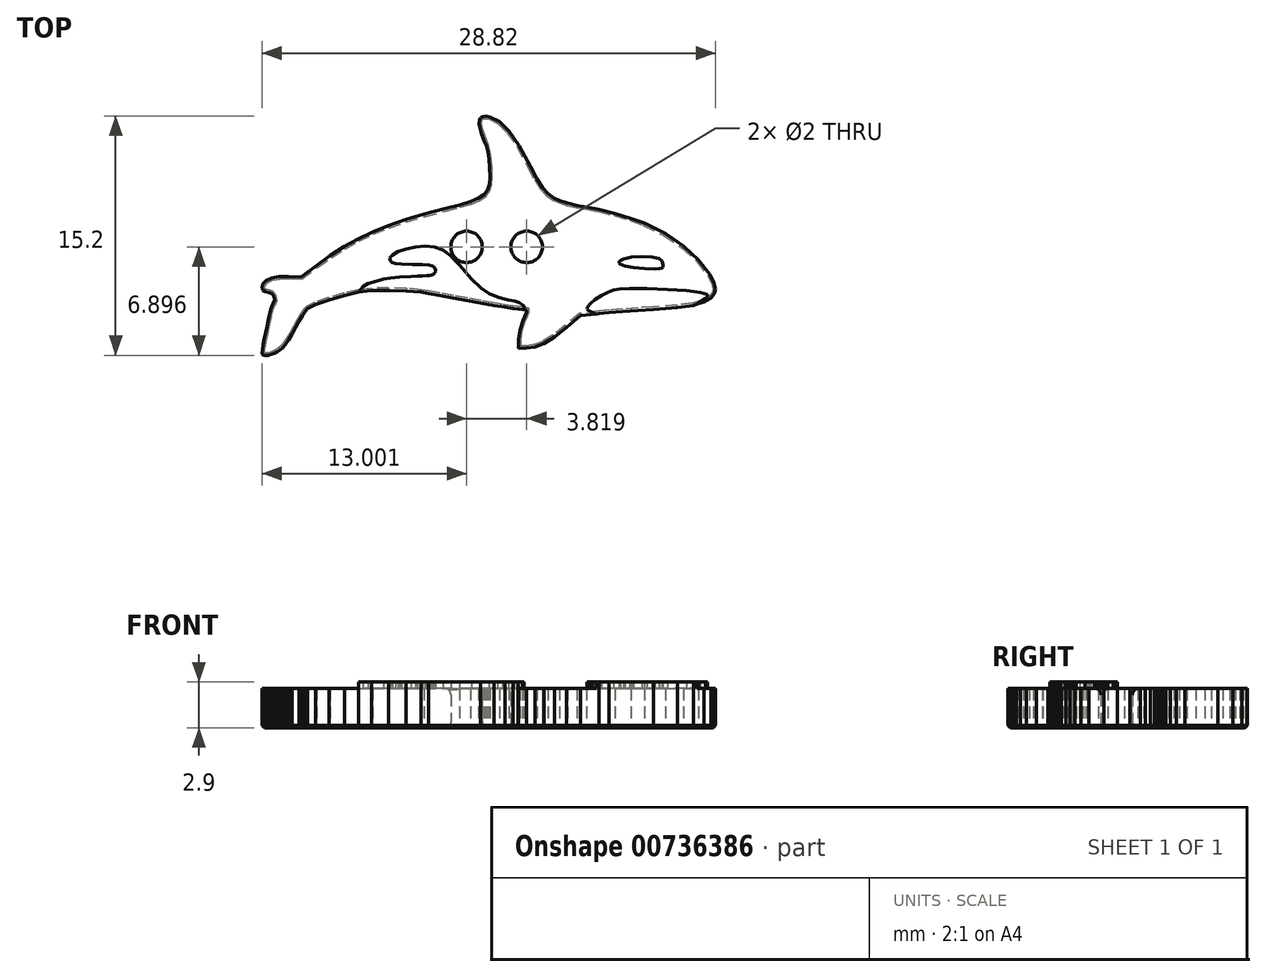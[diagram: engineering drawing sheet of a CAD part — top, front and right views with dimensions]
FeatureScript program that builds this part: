
annotation { "Feature Type Name" : "Feature", "Feature Type Description" : "" }
export const myFeature = defineFeature(function(context is Context, id is Id, definition is map)
    precondition{}
    {
        {
            var Q0;
            Q0=qCreatedBy(makeId("Top.planeOp"),FACE);
            var sketch = newSketch(context, id + "F0", { "sketchPlane" : qUnion([Q0])});
            skLineSegment(sketch, "E0", {"start": v(-14.38, -1.12) * mm, "end": v(-14.38, -1.01) * mm});
            skLineSegment(sketch, "E1", {"start": v(-14.38, -1.01) * mm, "end": v(-14.36, -0.8) * mm});
            skLineSegment(sketch, "E2", {"start": v(-14.36, -0.8) * mm, "end": v(-14.3, -0.5) * mm});
            skLineSegment(sketch, "E3", {"start": v(-14.3, -0.5) * mm, "end": v(-14.24, -0.16) * mm});
            skLineSegment(sketch, "E4", {"start": v(-14.24, -0.16) * mm, "end": v(-14.15, 0.22) * mm});
            skLineSegment(sketch, "E5", {"start": v(-14.15, 0.22) * mm, "end": v(-14.07, 0.63) * mm});
            skLineSegment(sketch, "E6", {"start": v(-14.07, 0.63) * mm, "end": v(-13.99, 1.01) * mm});
            skLineSegment(sketch, "E7", {"start": v(-13.99, 1.01) * mm, "end": v(-13.93, 1.32) * mm});
            skLineSegment(sketch, "E8", {"start": v(-13.93, 1.32) * mm, "end": v(-13.88, 1.57) * mm});
            skLineSegment(sketch, "E9", {"start": v(-13.88, 1.57) * mm, "end": v(-13.8, 1.8) * mm});
            skLineSegment(sketch, "E10", {"start": v(-13.8, 1.8) * mm, "end": v(-13.74, 1.98) * mm});
            skLineSegment(sketch, "E11", {"start": v(-13.74, 1.98) * mm, "end": v(-13.66, 2.1) * mm});
            skLineSegment(sketch, "E12", {"start": v(-13.66, 2.1) * mm, "end": v(-13.57, 2.32) * mm});
            skLineSegment(sketch, "E13", {"start": v(-13.57, 2.32) * mm, "end": v(-13.62, 2.55) * mm});
            skLineSegment(sketch, "E14", {"start": v(-13.62, 2.55) * mm, "end": v(-13.76, 2.74) * mm});
            skLineSegment(sketch, "E15", {"start": v(-13.76, 2.74) * mm, "end": v(-13.98, 2.82) * mm});
            skLineSegment(sketch, "E16", {"start": v(-13.98, 2.82) * mm, "end": v(-14.2, 2.86) * mm});
            skLineSegment(sketch, "E17", {"start": v(-14.2, 2.86) * mm, "end": v(-14.34, 2.98) * mm});
            skLineSegment(sketch, "E18", {"start": v(-14.34, 2.98) * mm, "end": v(-14.39, 3.14) * mm});
            skLineSegment(sketch, "E19", {"start": v(-14.39, 3.14) * mm, "end": v(-14.33, 3.34) * mm});
            skLineSegment(sketch, "E20", {"start": v(-14.33, 3.34) * mm, "end": v(-14.12, 3.58) * mm});
            skLineSegment(sketch, "E21", {"start": v(-14.12, 3.58) * mm, "end": v(-13.77, 3.74) * mm});
            skLineSegment(sketch, "E22", {"start": v(-13.77, 3.74) * mm, "end": v(-13.3, 3.83) * mm});
            skLineSegment(sketch, "E23", {"start": v(-13.3, 3.83) * mm, "end": v(-12.7, 3.84) * mm});
            skLineSegment(sketch, "E24", {"start": v(-12.7, 3.84) * mm, "end": v(-11.91, 3.8) * mm});
            skLineSegment(sketch, "E25", {"start": v(-11.91, 3.8) * mm, "end": v(-10.93, 4.53) * mm});
            skLineSegment(sketch, "E26", {"start": v(-10.93, 4.53) * mm, "end": v(-10.05, 5.16) * mm});
            skLineSegment(sketch, "E27", {"start": v(-10.05, 5.16) * mm, "end": v(-9.18, 5.71) * mm});
            skLineSegment(sketch, "E28", {"start": v(-9.18, 5.71) * mm, "end": v(-8.28, 6.2) * mm});
            skLineSegment(sketch, "E29", {"start": v(-8.28, 6.2) * mm, "end": v(-7.35, 6.65) * mm});
            skLineSegment(sketch, "E30", {"start": v(-7.35, 6.65) * mm, "end": v(-6.35, 7.06) * mm});
            skLineSegment(sketch, "E31", {"start": v(-6.35, 7.06) * mm, "end": v(-5.27, 7.43) * mm});
            skLineSegment(sketch, "E32", {"start": v(-5.27, 7.43) * mm, "end": v(-4.08, 7.79) * mm});
            skLineSegment(sketch, "E33", {"start": v(-4.08, 7.79) * mm, "end": v(-2.75, 8.13) * mm});
            skLineSegment(sketch, "E34", {"start": v(-2.75, 8.13) * mm, "end": v(-1.84, 8.37) * mm});
            skLineSegment(sketch, "E35", {"start": v(-1.84, 8.37) * mm, "end": v(-1.14, 8.58) * mm});
            skLineSegment(sketch, "E36", {"start": v(-1.14, 8.58) * mm, "end": v(-0.62, 8.8) * mm});
            skLineSegment(sketch, "E37", {"start": v(-0.62, 8.8) * mm, "end": v(-0.27, 9.03) * mm});
            skLineSegment(sketch, "E38", {"start": v(-0.27, 9.03) * mm, "end": v(-0.05, 9.32) * mm});
            skLineSegment(sketch, "E39", {"start": v(-0.05, 9.32) * mm, "end": v(0.06, 9.69) * mm});
            skLineSegment(sketch, "E40", {"start": v(0.06, 9.69) * mm, "end": v(0.1, 10.15) * mm});
            skLineSegment(sketch, "E41", {"start": v(0.1, 10.15) * mm, "end": v(0.07, 10.74) * mm});
            skLineSegment(sketch, "E42", {"start": v(0.07, 10.74) * mm, "end": v(0.02, 11.29) * mm});
            skLineSegment(sketch, "E43", {"start": v(0.02, 11.29) * mm, "end": v(-0.04, 11.72) * mm});
            skLineSegment(sketch, "E44", {"start": v(-0.04, 11.72) * mm, "end": v(-0.13, 12.1) * mm});
            skLineSegment(sketch, "E45", {"start": v(-0.13, 12.1) * mm, "end": v(-0.27, 12.45) * mm});
            skLineSegment(sketch, "E46", {"start": v(-0.27, 12.45) * mm, "end": v(-0.44, 12.88) * mm});
            skLineSegment(sketch, "E47", {"start": v(-0.44, 12.88) * mm, "end": v(-0.54, 13.24) * mm});
            skLineSegment(sketch, "E48", {"start": v(-0.54, 13.24) * mm, "end": v(-0.6, 13.53) * mm});
            skLineSegment(sketch, "E49", {"start": v(-0.6, 13.53) * mm, "end": v(-0.57, 13.76) * mm});
            skLineSegment(sketch, "E50", {"start": v(-0.57, 13.76) * mm, "end": v(-0.5, 13.9) * mm});
            skLineSegment(sketch, "E51", {"start": v(-0.5, 13.9) * mm, "end": v(-0.35, 14) * mm});
            skLineSegment(sketch, "E52", {"start": v(-0.35, 14) * mm, "end": v(-0.15, 14) * mm});
            skLineSegment(sketch, "E53", {"start": v(-0.15, 14) * mm, "end": v(0.12, 13.96) * mm});
            skLineSegment(sketch, "E54", {"start": v(0.12, 13.96) * mm, "end": v(0.71, 13.66) * mm});
            skLineSegment(sketch, "E55", {"start": v(0.71, 13.66) * mm, "end": v(1.3, 13.07) * mm});
            skLineSegment(sketch, "E56", {"start": v(1.3, 13.07) * mm, "end": v(1.94, 12.14) * mm});
            skLineSegment(sketch, "E57", {"start": v(1.94, 12.14) * mm, "end": v(2.66, 10.82) * mm});
            skLineSegment(sketch, "E58", {"start": v(2.66, 10.82) * mm, "end": v(3.08, 10.03) * mm});
            skLineSegment(sketch, "E59", {"start": v(3.08, 10.03) * mm, "end": v(3.43, 9.48) * mm});
            skLineSegment(sketch, "E60", {"start": v(3.43, 9.48) * mm, "end": v(3.77, 9.1) * mm});
            skLineSegment(sketch, "E61", {"start": v(3.77, 9.1) * mm, "end": v(4.17, 8.81) * mm});
            skLineSegment(sketch, "E62", {"start": v(4.17, 8.81) * mm, "end": v(4.53, 8.65) * mm});
            skLineSegment(sketch, "E63", {"start": v(4.53, 8.65) * mm, "end": v(5.03, 8.49) * mm});
            skLineSegment(sketch, "E64", {"start": v(5.03, 8.49) * mm, "end": v(5.62, 8.35) * mm});
            skLineSegment(sketch, "E65", {"start": v(5.62, 8.35) * mm, "end": v(6.24, 8.24) * mm});
            skLineSegment(sketch, "E66", {"start": v(6.24, 8.24) * mm, "end": v(7.05, 8.09) * mm});
            skLineSegment(sketch, "E67", {"start": v(7.05, 8.09) * mm, "end": v(8.05, 7.83) * mm});
            skLineSegment(sketch, "E68", {"start": v(8.05, 7.83) * mm, "end": v(9.07, 7.52) * mm});
            skLineSegment(sketch, "E69", {"start": v(9.07, 7.52) * mm, "end": v(9.9, 7.21) * mm});
            skLineSegment(sketch, "E70", {"start": v(9.9, 7.21) * mm, "end": v(11.23, 6.55) * mm});
            skLineSegment(sketch, "E71", {"start": v(11.23, 6.55) * mm, "end": v(12.4, 5.76) * mm});
            skLineSegment(sketch, "E72", {"start": v(12.4, 5.76) * mm, "end": v(13.35, 4.88) * mm});
            skLineSegment(sketch, "E73", {"start": v(13.35, 4.88) * mm, "end": v(14.06, 3.94) * mm});
            skLineSegment(sketch, "E74", {"start": v(14.06, 3.94) * mm, "end": v(14.33, 3.42) * mm});
            skLineSegment(sketch, "E75", {"start": v(14.33, 3.42) * mm, "end": v(14.43, 3.04) * mm});
            skLineSegment(sketch, "E76", {"start": v(14.43, 3.04) * mm, "end": v(14.36, 2.74) * mm});
            skLineSegment(sketch, "E77", {"start": v(14.36, 2.74) * mm, "end": v(14.13, 2.47) * mm});
            skLineSegment(sketch, "E78", {"start": v(14.13, 2.47) * mm, "end": v(13.68, 2.19) * mm});
            skLineSegment(sketch, "E79", {"start": v(13.68, 2.19) * mm, "end": v(13.01, 2) * mm});
            skLineSegment(sketch, "E80", {"start": v(13.01, 2) * mm, "end": v(12, 1.85) * mm});
            skLineSegment(sketch, "E81", {"start": v(12, 1.85) * mm, "end": v(10.47, 1.74) * mm});
            skLineSegment(sketch, "E82", {"start": v(10.47, 1.74) * mm, "end": v(9.5, 1.67) * mm});
            skLineSegment(sketch, "E83", {"start": v(9.5, 1.67) * mm, "end": v(8.52, 1.6) * mm});
            skLineSegment(sketch, "E84", {"start": v(8.52, 1.6) * mm, "end": v(7.66, 1.53) * mm});
            skLineSegment(sketch, "E85", {"start": v(7.66, 1.53) * mm, "end": v(7.03, 1.47) * mm});
            skLineSegment(sketch, "E86", {"start": v(7.03, 1.47) * mm, "end": v(5.85, 1.34) * mm});
            skLineSegment(sketch, "E87", {"start": v(5.85, 1.34) * mm, "end": v(4.96, 0.59) * mm});
            skLineSegment(sketch, "E88", {"start": v(4.96, 0.59) * mm, "end": v(4.2, -0.02) * mm});
            skLineSegment(sketch, "E89", {"start": v(4.2, -0.02) * mm, "end": v(3.54, -0.43) * mm});
            skLineSegment(sketch, "E90", {"start": v(3.54, -0.43) * mm, "end": v(2.97, -0.66) * mm});
            skLineSegment(sketch, "E91", {"start": v(2.97, -0.66) * mm, "end": v(2.43, -0.73) * mm});
            skLineSegment(sketch, "E92", {"start": v(2.43, -0.73) * mm, "end": v(1.91, -0.74) * mm});
            skLineSegment(sketch, "E93", {"start": v(1.91, -0.74) * mm, "end": v(1.92, -0.17) * mm});
            skLineSegment(sketch, "E94", {"start": v(1.92, -0.17) * mm, "end": v(2, 0.41) * mm});
            skLineSegment(sketch, "E95", {"start": v(2, 0.41) * mm, "end": v(2.2, 1.02) * mm});
            skLineSegment(sketch, "E96", {"start": v(2.2, 1.02) * mm, "end": v(2.3, 1.26) * mm});
            skLineSegment(sketch, "E97", {"start": v(2.3, 1.26) * mm, "end": v(2.37, 1.46) * mm});
            skLineSegment(sketch, "E98", {"start": v(2.37, 1.46) * mm, "end": v(2.42, 1.6) * mm});
            skLineSegment(sketch, "E99", {"start": v(2.42, 1.6) * mm, "end": v(2.42, 1.67) * mm});
            skLineSegment(sketch, "E100", {"start": v(2.42, 1.67) * mm, "end": v(2.34, 1.7) * mm});
            skLineSegment(sketch, "E101", {"start": v(2.34, 1.7) * mm, "end": v(2.15, 1.73) * mm});
            skLineSegment(sketch, "E102", {"start": v(2.15, 1.73) * mm, "end": v(1.88, 1.76) * mm});
            skLineSegment(sketch, "E103", {"start": v(1.88, 1.76) * mm, "end": v(1.55, 1.8) * mm});
            skLineSegment(sketch, "E104", {"start": v(1.55, 1.8) * mm, "end": v(1.06, 1.87) * mm});
            skLineSegment(sketch, "E105", {"start": v(1.06, 1.87) * mm, "end": v(0.35, 1.99) * mm});
            skLineSegment(sketch, "E106", {"start": v(0.35, 1.99) * mm, "end": v(-0.5, 2.13) * mm});
            skLineSegment(sketch, "E107", {"start": v(-0.5, 2.13) * mm, "end": v(-1.37, 2.3) * mm});
            skLineSegment(sketch, "E108", {"start": v(-1.37, 2.3) * mm, "end": v(-2.24, 2.46) * mm});
            skLineSegment(sketch, "E109", {"start": v(-2.24, 2.46) * mm, "end": v(-3.08, 2.62) * mm});
            skLineSegment(sketch, "E110", {"start": v(-3.08, 2.62) * mm, "end": v(-3.8, 2.75) * mm});
            skLineSegment(sketch, "E111", {"start": v(-3.8, 2.75) * mm, "end": v(-4.28, 2.83) * mm});
            skLineSegment(sketch, "E112", {"start": v(-4.28, 2.83) * mm, "end": v(-5.22, 2.92) * mm});
            skLineSegment(sketch, "E113", {"start": v(-5.22, 2.92) * mm, "end": v(-6.34, 2.95) * mm});
            skLineSegment(sketch, "E114", {"start": v(-6.34, 2.95) * mm, "end": v(-7.41, 2.92) * mm});
            skLineSegment(sketch, "E115", {"start": v(-7.41, 2.92) * mm, "end": v(-8.25, 2.83) * mm});
            skLineSegment(sketch, "E116", {"start": v(-8.25, 2.83) * mm, "end": v(-9.13, 2.63) * mm});
            skLineSegment(sketch, "E117", {"start": v(-9.13, 2.63) * mm, "end": v(-10.12, 2.33) * mm});
            skLineSegment(sketch, "E118", {"start": v(-10.12, 2.33) * mm, "end": v(-10.98, 2.03) * mm});
            skLineSegment(sketch, "E119", {"start": v(-10.98, 2.03) * mm, "end": v(-11.47, 1.8) * mm});
            skLineSegment(sketch, "E120", {"start": v(-11.47, 1.8) * mm, "end": v(-11.62, 1.63) * mm});
            skLineSegment(sketch, "E121", {"start": v(-11.62, 1.63) * mm, "end": v(-11.81, 1.35) * mm});
            skLineSegment(sketch, "E122", {"start": v(-11.81, 1.35) * mm, "end": v(-12.03, 0.98) * mm});
            skLineSegment(sketch, "E123", {"start": v(-12.03, 0.98) * mm, "end": v(-12.26, 0.58) * mm});
            skLineSegment(sketch, "E124", {"start": v(-12.26, 0.58) * mm, "end": v(-12.48, 0.16) * mm});
            skLineSegment(sketch, "E125", {"start": v(-12.48, 0.16) * mm, "end": v(-12.7, -0.22) * mm});
            skLineSegment(sketch, "E126", {"start": v(-12.7, -0.22) * mm, "end": v(-12.92, -0.52) * mm});
            skLineSegment(sketch, "E127", {"start": v(-12.92, -0.52) * mm, "end": v(-13.07, -0.71) * mm});
            skLineSegment(sketch, "E128", {"start": v(-13.07, -0.71) * mm, "end": v(-13.23, -0.85) * mm});
            skLineSegment(sketch, "E129", {"start": v(-13.23, -0.85) * mm, "end": v(-13.42, -0.96) * mm});
            skLineSegment(sketch, "E130", {"start": v(-13.42, -0.96) * mm, "end": v(-13.62, -1.06) * mm});
            skLineSegment(sketch, "E131", {"start": v(-13.62, -1.06) * mm, "end": v(-13.82, -1.13) * mm});
            skLineSegment(sketch, "E132", {"start": v(-13.82, -1.13) * mm, "end": v(-14, -1.18) * mm});
            skLineSegment(sketch, "E133", {"start": v(-14, -1.18) * mm, "end": v(-14.17, -1.2) * mm});
            skLineSegment(sketch, "E134", {"start": v(-14.17, -1.2) * mm, "end": v(-14.3, -1.17) * mm});
            skLineSegment(sketch, "E135", {"start": v(-14.3, -1.17) * mm, "end": v(-14.38, -1.12) * mm});
            skLineSegment(sketch, "E136", {"start": v(13.57, 2.29) * mm, "end": v(13.78, 2.44) * mm});
            skLineSegment(sketch, "E137", {"start": v(13.78, 2.44) * mm, "end": v(13.91, 2.57) * mm});
            skLineSegment(sketch, "E138", {"start": v(13.91, 2.57) * mm, "end": v(13.9, 2.67) * mm});
            skLineSegment(sketch, "E139", {"start": v(13.9, 2.67) * mm, "end": v(13.47, 2.8) * mm});
            skLineSegment(sketch, "E140", {"start": v(13.47, 2.8) * mm, "end": v(12.57, 2.92) * mm});
            skLineSegment(sketch, "E141", {"start": v(12.57, 2.92) * mm, "end": v(11.37, 3.01) * mm});
            skLineSegment(sketch, "E142", {"start": v(11.37, 3.01) * mm, "end": v(10.06, 3.05) * mm});
            skLineSegment(sketch, "E143", {"start": v(10.06, 3.05) * mm, "end": v(8.97, 3.06) * mm});
            skLineSegment(sketch, "E144", {"start": v(8.97, 3.06) * mm, "end": v(8.32, 3.04) * mm});
            skLineSegment(sketch, "E145", {"start": v(8.32, 3.04) * mm, "end": v(7.93, 2.98) * mm});
            skLineSegment(sketch, "E146", {"start": v(7.93, 2.98) * mm, "end": v(7.61, 2.85) * mm});
            skLineSegment(sketch, "E147", {"start": v(7.61, 2.85) * mm, "end": v(7.18, 2.62) * mm});
            skLineSegment(sketch, "E148", {"start": v(7.18, 2.62) * mm, "end": v(6.78, 2.36) * mm});
            skLineSegment(sketch, "E149", {"start": v(6.78, 2.36) * mm, "end": v(6.47, 2.1) * mm});
            skLineSegment(sketch, "E150", {"start": v(6.47, 2.1) * mm, "end": v(6.29, 1.88) * mm});
            skLineSegment(sketch, "E151", {"start": v(6.29, 1.88) * mm, "end": v(6.25, 1.77) * mm});
            skLineSegment(sketch, "E152", {"start": v(6.25, 1.77) * mm, "end": v(6.3, 1.72) * mm});
            skLineSegment(sketch, "E153", {"start": v(1.93, 2.16) * mm, "end": v(1.67, 2.26) * mm});
            skLineSegment(sketch, "E154", {"start": v(1.67, 2.26) * mm, "end": v(1.29, 2.34) * mm});
            skLineSegment(sketch, "E155", {"start": v(1.29, 2.34) * mm, "end": v(0.9, 2.44) * mm});
            skLineSegment(sketch, "E156", {"start": v(0.9, 2.44) * mm, "end": v(0.57, 2.53) * mm});
            skLineSegment(sketch, "E157", {"start": v(0.57, 2.53) * mm, "end": v(0.04, 2.75) * mm});
            skLineSegment(sketch, "E158", {"start": v(0.04, 2.75) * mm, "end": v(-0.47, 3.1) * mm});
            skLineSegment(sketch, "E159", {"start": v(-0.47, 3.1) * mm, "end": v(-1.06, 3.67) * mm});
            skLineSegment(sketch, "E160", {"start": v(-1.06, 3.67) * mm, "end": v(-1.83, 4.55) * mm});
            skLineSegment(sketch, "E161", {"start": v(-1.83, 4.55) * mm, "end": v(-2.38, 5.12) * mm});
            skLineSegment(sketch, "E162", {"start": v(-2.38, 5.12) * mm, "end": v(-2.89, 5.49) * mm});
            skLineSegment(sketch, "E163", {"start": v(-2.89, 5.49) * mm, "end": v(-3.42, 5.69) * mm});
            skLineSegment(sketch, "E164", {"start": v(-3.42, 5.69) * mm, "end": v(-4.01, 5.75) * mm});
            skLineSegment(sketch, "E165", {"start": v(-4.01, 5.75) * mm, "end": v(-4.62, 5.7) * mm});
            skLineSegment(sketch, "E166", {"start": v(-4.62, 5.7) * mm, "end": v(-5.22, 5.58) * mm});
            skLineSegment(sketch, "E167", {"start": v(-5.22, 5.58) * mm, "end": v(-5.73, 5.4) * mm});
            skLineSegment(sketch, "E168", {"start": v(-5.73, 5.4) * mm, "end": v(-6.1, 5.2) * mm});
            skLineSegment(sketch, "E169", {"start": v(-6.1, 5.2) * mm, "end": v(-6.27, 5) * mm});
            skLineSegment(sketch, "E170", {"start": v(-6.27, 5) * mm, "end": v(-6.23, 4.81) * mm});
            skLineSegment(sketch, "E171", {"start": v(-6.23, 4.81) * mm, "end": v(-6.12, 4.72) * mm});
            skLineSegment(sketch, "E172", {"start": v(-6.12, 4.72) * mm, "end": v(-5.9, 4.65) * mm});
            skLineSegment(sketch, "E173", {"start": v(-5.9, 4.65) * mm, "end": v(-5.5, 4.62) * mm});
            skLineSegment(sketch, "E174", {"start": v(-5.5, 4.62) * mm, "end": v(-4.84, 4.6) * mm});
            skLineSegment(sketch, "E175", {"start": v(-4.84, 4.6) * mm, "end": v(-4.2, 4.58) * mm});
            skLineSegment(sketch, "E176", {"start": v(-4.2, 4.58) * mm, "end": v(-3.78, 4.54) * mm});
            skLineSegment(sketch, "E177", {"start": v(-3.78, 4.54) * mm, "end": v(-3.55, 4.49) * mm});
            skLineSegment(sketch, "E178", {"start": v(-3.55, 4.49) * mm, "end": v(-3.43, 4.4) * mm});
            skLineSegment(sketch, "E179", {"start": v(-3.43, 4.4) * mm, "end": v(-3.36, 4.23) * mm});
            skLineSegment(sketch, "E180", {"start": v(-3.36, 4.23) * mm, "end": v(-3.4, 4.06) * mm});
            skLineSegment(sketch, "E181", {"start": v(-3.4, 4.06) * mm, "end": v(-3.44, 4) * mm});
            skLineSegment(sketch, "E182", {"start": v(-3.44, 4) * mm, "end": v(-3.5, 3.96) * mm});
            skLineSegment(sketch, "E183", {"start": v(-3.5, 3.96) * mm, "end": v(-3.6, 3.93) * mm});
            skLineSegment(sketch, "E184", {"start": v(-3.6, 3.93) * mm, "end": v(-3.74, 3.9) * mm});
            skLineSegment(sketch, "E185", {"start": v(-3.74, 3.9) * mm, "end": v(-3.93, 3.88) * mm});
            skLineSegment(sketch, "E186", {"start": v(-3.93, 3.88) * mm, "end": v(-4.18, 3.86) * mm});
            skLineSegment(sketch, "E187", {"start": v(-4.18, 3.86) * mm, "end": v(-4.5, 3.84) * mm});
            skLineSegment(sketch, "E188", {"start": v(-4.5, 3.84) * mm, "end": v(-4.92, 3.83) * mm});
            skLineSegment(sketch, "E189", {"start": v(-4.92, 3.83) * mm, "end": v(-5.65, 3.8) * mm});
            skLineSegment(sketch, "E190", {"start": v(-5.65, 3.8) * mm, "end": v(-6.2, 3.74) * mm});
            skLineSegment(sketch, "E191", {"start": v(-6.2, 3.74) * mm, "end": v(-6.65, 3.66) * mm});
            skLineSegment(sketch, "E192", {"start": v(-6.65, 3.66) * mm, "end": v(-7.06, 3.53) * mm});
            skLineSegment(sketch, "E193", {"start": v(-7.06, 3.53) * mm, "end": v(-7.65, 3.36) * mm});
            skLineSegment(sketch, "E194", {"start": v(11.1, 4.57) * mm, "end": v(11.03, 4.8) * mm});
            skLineSegment(sketch, "E195", {"start": v(11.03, 4.8) * mm, "end": v(10.83, 4.96) * mm});
            skLineSegment(sketch, "E196", {"start": v(10.83, 4.96) * mm, "end": v(10.4, 5.06) * mm});
            skLineSegment(sketch, "E197", {"start": v(10.4, 5.06) * mm, "end": v(9.75, 5.09) * mm});
            skLineSegment(sketch, "E198", {"start": v(9.75, 5.09) * mm, "end": v(9.09, 5.04) * mm});
            skLineSegment(sketch, "E199", {"start": v(9.09, 5.04) * mm, "end": v(8.6, 4.93) * mm});
            skLineSegment(sketch, "E200", {"start": v(8.6, 4.93) * mm, "end": v(8.4, 4.85) * mm});
            skLineSegment(sketch, "E201", {"start": v(8.4, 4.85) * mm, "end": v(8.3, 4.78) * mm});
            skLineSegment(sketch, "E202", {"start": v(8.3, 4.78) * mm, "end": v(8.3, 4.7) * mm});
            skLineSegment(sketch, "E203", {"start": v(8.3, 4.7) * mm, "end": v(8.37, 4.62) * mm});
            skLineSegment(sketch, "E204", {"start": v(8.37, 4.62) * mm, "end": v(8.67, 4.5) * mm});
            skLineSegment(sketch, "E205", {"start": v(8.67, 4.5) * mm, "end": v(9.23, 4.4) * mm});
            skLineSegment(sketch, "E206", {"start": v(9.23, 4.4) * mm, "end": v(9.9, 4.32) * mm});
            skLineSegment(sketch, "E207", {"start": v(9.9, 4.32) * mm, "end": v(10.58, 4.3) * mm});
            skLineSegment(sketch, "E208", {"start": v(10.58, 4.3) * mm, "end": v(10.86, 4.32) * mm});
            skLineSegment(sketch, "E209", {"start": v(10.86, 4.32) * mm, "end": v(11.01, 4.35) * mm});
            skLineSegment(sketch, "E210", {"start": v(11.01, 4.35) * mm, "end": v(11.08, 4.43) * mm});
            skLineSegment(sketch, "E211", {"start": v(11.08, 4.43) * mm, "end": v(11.1, 4.57) * mm});
            skLineSegment(sketch, "E212", {"start": v(-7.65, 3.36) * mm, "end": v(-7.96, 3.19) * mm});
            skLineSegment(sketch, "E213", {"start": v(-8.25, 2.83) * mm, "end": v(-7.96, 3.19) * mm});
            skLineSegment(sketch, "E214", {"start": v(1.93, 2.16) * mm, "end": v(2.15, 2.06) * mm});
            skLineSegment(sketch, "E215", {"start": v(2.15, 2.06) * mm, "end": v(2.26, 1.94) * mm});
            skLineSegment(sketch, "E216", {"start": v(2.26, 1.94) * mm, "end": v(2.27, 1.82) * mm});
            skLineSegment(sketch, "E217", {"start": v(2.27, 1.82) * mm, "end": v(2.15, 1.73) * mm});
            skLineSegment(sketch, "E218", {"start": v(6.3, 1.72) * mm, "end": v(6.43, 1.62) * mm});
            skLineSegment(sketch, "E219", {"start": v(6.43, 1.62) * mm, "end": v(6.61, 1.54) * mm});
            skLineSegment(sketch, "E220", {"start": v(6.61, 1.54) * mm, "end": v(6.87, 1.45) * mm});
            skLineSegment(sketch, "E221", {"start": v(13.57, 2.29) * mm, "end": v(13.34, 2.13) * mm});
            skPoint(sketch, "E221.endSnap0", {"position": v(13.34, 2.1) * mm});
            skLineSegment(sketch, "E222", {"start": v(13.34, 2.13) * mm, "end": v(13.26, 2.06) * mm});
            skCircle(sketch, "E223", {"center": v(0, -1) * mm, "radius": 15 * mm, "construction": true});
            skPoint(sketch, "E223.third.point", {"position": v(-14.33, 3.42) * mm});
            skLineSegment(sketch, "E224", {"start": v(-16.63, -2.36) * mm, "end": v(17.74, -2.36) * mm, "construction": true});
            skLineSegment(sketch, "E225", {"start": v(14.43, 7.5) * mm, "end": v(14.43, -2.36) * mm, "construction": true});
            skLineSegment(sketch, "E226", {"start": v(-14.39, -2.52) * mm, "end": v(-14.39, 4.2) * mm, "construction": true});
            skCircle(sketch, "E227", {"center": v(1.8, 5.7) * mm, "radius": 3.91 * mm});
            skLineSegment(sketch, "E228", {"start": v(-17.57, 5.7) * mm, "end": v(16.86, 5.7) * mm, "construction": true});
            skCircle(sketch, "E229", {"center": v(2.43, 5.7) * mm, "radius": 1 * mm});
            skCircle(sketch, "E230", {"center": v(-1.39, 5.7) * mm, "radius": 1 * mm});
            skSolve(sketch);
        }
        {
            var Q0;
            {var subQ1=sQuery(id+"F0.wireOp",EDGE,"E80");Q0=makeQuery(id+"F0.imprint","IMPRINT",FACE,{"disambiguationData":[TD([[makeQuery(id+"F0.imprint","IMPRINT",EDGE,{"derivedFrom":subQ1}),-1.0]])]});}
            var Q1;
            Q1=makeQuery(id+"F0.imprint","IMPRINT",FACE,{"disambiguationData":[TD([[makeQuery(id+"F0.imprint","IMPRINT",EDGE,{"derivedFrom":sQuery(id+"F0.wireOp",EDGE,"E102")}),-1.0]])]});
            var Q2;
            Q2=makeQuery(id+"F0.imprint","IMPRINT",FACE,{"disambiguationData":[TD([[makeQuery(id+"F0.imprint","IMPRINT",EDGE,{"derivedFrom":sQuery(id+"F0.wireOp",EDGE,"E0")}),-1.0]])]});
            var Q3;
            Q3=makeQuery(id+"F0.imprint","IMPRINT",FACE,{"disambiguationData":[TD([[makeQuery(id+"F0.imprint","IMPRINT",EDGE,{"derivedFrom":sQuery(id+"F0.wireOp",EDGE,"E194")}),1.0]])]});
            var Q4;
            Q4=makeQuery(id+"F0.imprint","IMPRINT",FACE,{"disambiguationData":[TD([[makeQuery(id+"F0.imprint","IMPRINT",EDGE,{"derivedFrom":sQuery(id+"F0.wireOp",EDGE,"E153")}),-1.0]])]});
            var Q5;
            {var subQ0=sQuery(id+"F0.wireOp",EDGE,"E106");Q5=makeQuery(id+"F0.imprint","IMPRINT",FACE,{"disambiguationData":[TD([[makeQuery(id+"F0.imprint","IMPRINT",EDGE,{"derivedFrom":subQ0}),-1.0]])]});}
            var Q6;
            {var subQ1=sQuery(id+"F0.wireOp",EDGE,"E62");Q6=makeQuery(id+"F0.imprint","IMPRINT",FACE,{"disambiguationData":[TD([[makeQuery(id+"F0.imprint","IMPRINT",EDGE,{"derivedFrom":subQ1}),-1.0]])]});}
            var Q7;
            {var subQ1=sQuery(id+"F0.wireOp",EDGE,"E104");Q7=makeQuery(id+"F0.imprint","IMPRINT",FACE,{"disambiguationData":[TD([[makeQuery(id+"F0.imprint","IMPRINT",EDGE,{"derivedFrom":subQ1}),-1.0]])]});}
            var Q8;
            {var subQ0=sQuery(id+"F0.wireOp",EDGE,"E38");Q8=makeQuery(id+"F0.imprint","IMPRINT",FACE,{"disambiguationData":[TD([[makeQuery(id+"F0.imprint","IMPRINT",EDGE,{"derivedFrom":subQ0}),-1.0]])]});}
            extrude(context, id + "F1", {"entities" : qUnion([Q0, Q1, Q2, Q3, Q4, Q5, Q6, Q7, Q8]), "depth" : 2.5 * mm, "offsetDistance" : 25 * mm});
        }
        {
            var Q0;
            Q0=makeQuery(id+"F1.opExtrude","CAP_FACE",FACE,{"disambiguationData":[OSD([sQuery(id+"F0.wireOp",EDGE,"E0"),sQuery(id+"F0.wireOp",EDGE,"E1"),sQuery(id+"F0.wireOp",EDGE,"E2"),sQuery(id+"F0.wireOp",EDGE,"E3"),sQuery(id+"F0.wireOp",EDGE,"E4"),sQuery(id+"F0.wireOp",EDGE,"E5"),sQuery(id+"F0.wireOp",EDGE,"E6"),sQuery(id+"F0.wireOp",EDGE,"E7"),sQuery(id+"F0.wireOp",EDGE,"E8"),sQuery(id+"F0.wireOp",EDGE,"E9"),sQuery(id+"F0.wireOp",EDGE,"E10"),sQuery(id+"F0.wireOp",EDGE,"E11"),sQuery(id+"F0.wireOp",EDGE,"E12"),sQuery(id+"F0.wireOp",EDGE,"E13"),sQuery(id+"F0.wireOp",EDGE,"E14"),sQuery(id+"F0.wireOp",EDGE,"E15"),sQuery(id+"F0.wireOp",EDGE,"E16"),sQuery(id+"F0.wireOp",EDGE,"E17"),sQuery(id+"F0.wireOp",EDGE,"E18"),sQuery(id+"F0.wireOp",EDGE,"E19"),sQuery(id+"F0.wireOp",EDGE,"E20"),sQuery(id+"F0.wireOp",EDGE,"E21"),sQuery(id+"F0.wireOp",EDGE,"E22"),sQuery(id+"F0.wireOp",EDGE,"E23"),sQuery(id+"F0.wireOp",EDGE,"E24"),sQuery(id+"F0.wireOp",EDGE,"E25"),sQuery(id+"F0.wireOp",EDGE,"E26"),sQuery(id+"F0.wireOp",EDGE,"E27"),sQuery(id+"F0.wireOp",EDGE,"E28"),sQuery(id+"F0.wireOp",EDGE,"E29"),sQuery(id+"F0.wireOp",EDGE,"E30"),sQuery(id+"F0.wireOp",EDGE,"E31"),sQuery(id+"F0.wireOp",EDGE,"E32"),sQuery(id+"F0.wireOp",EDGE,"E33"),sQuery(id+"F0.wireOp",EDGE,"E34"),sQuery(id+"F0.wireOp",EDGE,"E35"),sQuery(id+"F0.wireOp",EDGE,"E36"),sQuery(id+"F0.wireOp",EDGE,"E37"),sQuery(id+"F0.wireOp",EDGE,"E38"),sQuery(id+"F0.wireOp",EDGE,"E39"),sQuery(id+"F0.wireOp",EDGE,"E40"),sQuery(id+"F0.wireOp",EDGE,"E41"),sQuery(id+"F0.wireOp",EDGE,"E42"),sQuery(id+"F0.wireOp",EDGE,"E43"),sQuery(id+"F0.wireOp",EDGE,"E44"),sQuery(id+"F0.wireOp",EDGE,"E45"),sQuery(id+"F0.wireOp",EDGE,"E46"),sQuery(id+"F0.wireOp",EDGE,"E47"),sQuery(id+"F0.wireOp",EDGE,"E48"),sQuery(id+"F0.wireOp",EDGE,"E49"),sQuery(id+"F0.wireOp",EDGE,"E50"),sQuery(id+"F0.wireOp",EDGE,"E51"),sQuery(id+"F0.wireOp",EDGE,"E52"),sQuery(id+"F0.wireOp",EDGE,"E53"),sQuery(id+"F0.wireOp",EDGE,"E54"),sQuery(id+"F0.wireOp",EDGE,"E55"),sQuery(id+"F0.wireOp",EDGE,"E56"),sQuery(id+"F0.wireOp",EDGE,"E57"),sQuery(id+"F0.wireOp",EDGE,"E58"),sQuery(id+"F0.wireOp",EDGE,"E59"),sQuery(id+"F0.wireOp",EDGE,"E60"),sQuery(id+"F0.wireOp",EDGE,"E61"),sQuery(id+"F0.wireOp",EDGE,"E62"),sQuery(id+"F0.wireOp",EDGE,"E63"),sQuery(id+"F0.wireOp",EDGE,"E64"),sQuery(id+"F0.wireOp",EDGE,"E65"),sQuery(id+"F0.wireOp",EDGE,"E66"),sQuery(id+"F0.wireOp",EDGE,"E67"),sQuery(id+"F0.wireOp",EDGE,"E68"),sQuery(id+"F0.wireOp",EDGE,"E69"),sQuery(id+"F0.wireOp",EDGE,"E70"),sQuery(id+"F0.wireOp",EDGE,"E71"),sQuery(id+"F0.wireOp",EDGE,"E72"),sQuery(id+"F0.wireOp",EDGE,"E73"),sQuery(id+"F0.wireOp",EDGE,"E74"),sQuery(id+"F0.wireOp",EDGE,"E75"),sQuery(id+"F0.wireOp",EDGE,"E76"),sQuery(id+"F0.wireOp",EDGE,"E77"),sQuery(id+"F0.wireOp",EDGE,"E78"),sQuery(id+"F0.wireOp",EDGE,"E79"),sQuery(id+"F0.wireOp",EDGE,"E80"),sQuery(id+"F0.wireOp",EDGE,"E81"),sQuery(id+"F0.wireOp",EDGE,"E82"),sQuery(id+"F0.wireOp",EDGE,"E83"),sQuery(id+"F0.wireOp",EDGE,"E84"),sQuery(id+"F0.wireOp",EDGE,"E85"),sQuery(id+"F0.wireOp",EDGE,"E86"),sQuery(id+"F0.wireOp",EDGE,"E87"),sQuery(id+"F0.wireOp",EDGE,"E88"),sQuery(id+"F0.wireOp",EDGE,"E89"),sQuery(id+"F0.wireOp",EDGE,"E90"),sQuery(id+"F0.wireOp",EDGE,"E91"),sQuery(id+"F0.wireOp",EDGE,"E92"),sQuery(id+"F0.wireOp",EDGE,"E93"),sQuery(id+"F0.wireOp",EDGE,"E94"),sQuery(id+"F0.wireOp",EDGE,"E95"),sQuery(id+"F0.wireOp",EDGE,"E96"),sQuery(id+"F0.wireOp",EDGE,"E97"),sQuery(id+"F0.wireOp",EDGE,"E98"),sQuery(id+"F0.wireOp",EDGE,"E99"),sQuery(id+"F0.wireOp",EDGE,"E100"),sQuery(id+"F0.wireOp",EDGE,"E101"),sQuery(id+"F0.wireOp",EDGE,"E102"),sQuery(id+"F0.wireOp",EDGE,"E103"),sQuery(id+"F0.wireOp",EDGE,"E104"),sQuery(id+"F0.wireOp",EDGE,"E105"),sQuery(id+"F0.wireOp",EDGE,"E106"),sQuery(id+"F0.wireOp",EDGE,"E107"),sQuery(id+"F0.wireOp",EDGE,"E108"),sQuery(id+"F0.wireOp",EDGE,"E109"),sQuery(id+"F0.wireOp",EDGE,"E110"),sQuery(id+"F0.wireOp",EDGE,"E111"),sQuery(id+"F0.wireOp",EDGE,"E112"),sQuery(id+"F0.wireOp",EDGE,"E113"),sQuery(id+"F0.wireOp",EDGE,"E114"),sQuery(id+"F0.wireOp",EDGE,"E115"),sQuery(id+"F0.wireOp",EDGE,"E116"),sQuery(id+"F0.wireOp",EDGE,"E117"),sQuery(id+"F0.wireOp",EDGE,"E118"),sQuery(id+"F0.wireOp",EDGE,"E119"),sQuery(id+"F0.wireOp",EDGE,"E120"),sQuery(id+"F0.wireOp",EDGE,"E121"),sQuery(id+"F0.wireOp",EDGE,"E122"),sQuery(id+"F0.wireOp",EDGE,"E123"),sQuery(id+"F0.wireOp",EDGE,"E124"),sQuery(id+"F0.wireOp",EDGE,"E125"),sQuery(id+"F0.wireOp",EDGE,"E126"),sQuery(id+"F0.wireOp",EDGE,"E127"),sQuery(id+"F0.wireOp",EDGE,"E128"),sQuery(id+"F0.wireOp",EDGE,"E129"),sQuery(id+"F0.wireOp",EDGE,"E130"),sQuery(id+"F0.wireOp",EDGE,"E131"),sQuery(id+"F0.wireOp",EDGE,"E132"),sQuery(id+"F0.wireOp",EDGE,"E133"),sQuery(id+"F0.wireOp",EDGE,"E134"),sQuery(id+"F0.wireOp",EDGE,"E135")])],"isStart":false});
            var sketch = newSketch(context, id + "F2", { "sketchPlane" : qUnion([Q0])});
            skLineSegment(sketch, "E231.0", {"start": v(2.27, 1.82) * mm, "end": v(2.15, 1.73) * mm});
            skLineSegment(sketch, "E232.0", {"start": v(2.26, 1.94) * mm, "end": v(2.27, 1.82) * mm});
            skLineSegment(sketch, "E233.0", {"start": v(2.15, 2.06) * mm, "end": v(2.26, 1.94) * mm});
            skLineSegment(sketch, "E234.0", {"start": v(1.93, 2.16) * mm, "end": v(2.15, 2.06) * mm});
            skLineSegment(sketch, "E234.3", {"start": v(1.93, 2.16) * mm, "end": v(1.67, 2.26) * mm});
            skLineSegment(sketch, "E234.4", {"start": v(1.67, 2.26) * mm, "end": v(1.29, 2.34) * mm});
            skPoint(sketch, "E234.5", {"position": v(0.9, 2.44) * mm});
            skPoint(sketch, "E234.6", {"position": v(1.48, 2.3) * mm});
            skPoint(sketch, "E234.7", {"position": v(1.1, 2.39) * mm});
            skLineSegment(sketch, "E235.1", {"start": v(1.29, 2.34) * mm, "end": v(0.9, 2.44) * mm});
            skLineSegment(sketch, "E235.2", {"start": v(0.9, 2.44) * mm, "end": v(0.57, 2.53) * mm});
            skLineSegment(sketch, "E235.3", {"start": v(0.57, 2.53) * mm, "end": v(0.04, 2.75) * mm});
            skLineSegment(sketch, "E235.4", {"start": v(0.04, 2.75) * mm, "end": v(-0.47, 3.1) * mm});
            skLineSegment(sketch, "E235.5", {"start": v(-0.47, 3.1) * mm, "end": v(-1.06, 3.67) * mm});
            skLineSegment(sketch, "E235.6", {"start": v(-1.06, 3.67) * mm, "end": v(-1.83, 4.55) * mm});
            skLineSegment(sketch, "E235.7", {"start": v(-1.83, 4.55) * mm, "end": v(-2.38, 5.12) * mm});
            skLineSegment(sketch, "E235.8", {"start": v(-2.38, 5.12) * mm, "end": v(-2.89, 5.49) * mm});
            skLineSegment(sketch, "E235.9", {"start": v(-2.89, 5.49) * mm, "end": v(-3.42, 5.69) * mm});
            skLineSegment(sketch, "E235.10", {"start": v(-3.42, 5.69) * mm, "end": v(-4.01, 5.75) * mm});
            skLineSegment(sketch, "E235.11", {"start": v(-4.01, 5.75) * mm, "end": v(-4.62, 5.7) * mm});
            skLineSegment(sketch, "E235.12", {"start": v(-4.62, 5.7) * mm, "end": v(-5.22, 5.58) * mm});
            skLineSegment(sketch, "E235.13", {"start": v(-5.22, 5.58) * mm, "end": v(-5.73, 5.4) * mm});
            skLineSegment(sketch, "E235.14", {"start": v(-5.73, 5.4) * mm, "end": v(-6.1, 5.2) * mm});
            skLineSegment(sketch, "E235.15", {"start": v(-6.1, 5.2) * mm, "end": v(-6.27, 5) * mm});
            skLineSegment(sketch, "E235.16", {"start": v(-6.27, 5) * mm, "end": v(-6.23, 4.81) * mm});
            skLineSegment(sketch, "E235.17", {"start": v(-6.12, 4.72) * mm, "end": v(-5.9, 4.65) * mm});
            skLineSegment(sketch, "E235.18", {"start": v(-6.23, 4.81) * mm, "end": v(-6.12, 4.72) * mm});
            skLineSegment(sketch, "E235.19", {"start": v(-5.9, 4.65) * mm, "end": v(-5.5, 4.62) * mm});
            skLineSegment(sketch, "E235.20", {"start": v(-5.5, 4.62) * mm, "end": v(-4.84, 4.6) * mm});
            skLineSegment(sketch, "E235.21", {"start": v(-4.84, 4.6) * mm, "end": v(-4.2, 4.58) * mm});
            skLineSegment(sketch, "E235.22", {"start": v(-4.2, 4.58) * mm, "end": v(-3.78, 4.54) * mm});
            skLineSegment(sketch, "E235.23", {"start": v(-3.78, 4.54) * mm, "end": v(-3.55, 4.49) * mm});
            skLineSegment(sketch, "E235.24", {"start": v(-3.55, 4.49) * mm, "end": v(-3.43, 4.4) * mm});
            skLineSegment(sketch, "E235.25", {"start": v(-3.43, 4.4) * mm, "end": v(-3.36, 4.23) * mm});
            skLineSegment(sketch, "E235.26", {"start": v(-3.36, 4.23) * mm, "end": v(-3.4, 4.06) * mm});
            skLineSegment(sketch, "E235.27", {"start": v(-3.4, 4.06) * mm, "end": v(-3.44, 4) * mm});
            skLineSegment(sketch, "E235.28", {"start": v(-3.44, 4) * mm, "end": v(-3.5, 3.96) * mm});
            skLineSegment(sketch, "E235.29", {"start": v(-3.5, 3.96) * mm, "end": v(-3.6, 3.93) * mm});
            skLineSegment(sketch, "E235.30", {"start": v(-3.6, 3.93) * mm, "end": v(-3.74, 3.9) * mm});
            skLineSegment(sketch, "E235.31", {"start": v(-3.74, 3.9) * mm, "end": v(-3.93, 3.88) * mm});
            skLineSegment(sketch, "E235.32", {"start": v(-3.93, 3.88) * mm, "end": v(-4.18, 3.86) * mm});
            skLineSegment(sketch, "E235.33", {"start": v(-4.18, 3.86) * mm, "end": v(-4.5, 3.84) * mm});
            skLineSegment(sketch, "E235.34", {"start": v(-4.5, 3.84) * mm, "end": v(-4.92, 3.83) * mm});
            skLineSegment(sketch, "E235.35", {"start": v(-4.92, 3.83) * mm, "end": v(-5.65, 3.8) * mm});
            skLineSegment(sketch, "E235.36", {"start": v(-5.65, 3.8) * mm, "end": v(-6.2, 3.74) * mm});
            skLineSegment(sketch, "E235.37", {"start": v(-6.2, 3.74) * mm, "end": v(-6.65, 3.66) * mm});
            skLineSegment(sketch, "E235.38", {"start": v(-6.65, 3.66) * mm, "end": v(-7.06, 3.53) * mm});
            skLineSegment(sketch, "E235.39", {"start": v(-7.06, 3.53) * mm, "end": v(-7.65, 3.36) * mm});
            skLineSegment(sketch, "E235.40", {"start": v(-7.65, 3.36) * mm, "end": v(-7.96, 3.19) * mm});
            skLineSegment(sketch, "E235.41", {"start": v(-8.25, 2.83) * mm, "end": v(-7.96, 3.19) * mm});
            skLineSegment(sketch, "E235.42", {"start": v(-7.41, 2.92) * mm, "end": v(-8.25, 2.83) * mm});
            skLineSegment(sketch, "E235.43", {"start": v(-6.34, 2.95) * mm, "end": v(-7.41, 2.92) * mm});
            skLineSegment(sketch, "E235.44", {"start": v(-5.22, 2.92) * mm, "end": v(-6.34, 2.95) * mm});
            skLineSegment(sketch, "E235.45", {"start": v(-4.28, 2.83) * mm, "end": v(-5.22, 2.92) * mm});
            skLineSegment(sketch, "E235.46", {"start": v(-3.8, 2.75) * mm, "end": v(-4.28, 2.83) * mm});
            skLineSegment(sketch, "E235.47", {"start": v(-3.08, 2.62) * mm, "end": v(-3.8, 2.75) * mm});
            skLineSegment(sketch, "E235.48", {"start": v(-2.24, 2.46) * mm, "end": v(-3.08, 2.62) * mm});
            skLineSegment(sketch, "E235.49", {"start": v(-1.37, 2.3) * mm, "end": v(-2.24, 2.46) * mm});
            skLineSegment(sketch, "E235.50", {"start": v(-0.5, 2.13) * mm, "end": v(-1.37, 2.3) * mm});
            skLineSegment(sketch, "E235.51", {"start": v(0.35, 1.99) * mm, "end": v(-0.5, 2.13) * mm});
            skLineSegment(sketch, "E235.52", {"start": v(1.06, 1.87) * mm, "end": v(0.35, 1.99) * mm});
            skLineSegment(sketch, "E235.53", {"start": v(1.55, 1.8) * mm, "end": v(1.06, 1.87) * mm});
            skLineSegment(sketch, "E235.54", {"start": v(1.88, 1.76) * mm, "end": v(1.55, 1.8) * mm});
            skLineSegment(sketch, "E235.55", {"start": v(2.15, 1.73) * mm, "end": v(1.88, 1.76) * mm});
            skPoint(sketch, "E235.61", {"position": v(-3.15, 5.59) * mm});
            skPoint(sketch, "E235.62", {"position": v(-3.72, 5.72) * mm});
            skPoint(sketch, "E235.63", {"position": v(-4.04, 2.79) * mm});
            skPoint(sketch, "E235.64", {"position": v(2.27, 1.88) * mm});
            skLineSegment(sketch, "E236.0", {"start": v(9.23, 4.4) * mm, "end": v(9.9, 4.32) * mm});
            skLineSegment(sketch, "E236.1", {"start": v(11.37, 3.01) * mm, "end": v(10.06, 3.05) * mm});
            skLineSegment(sketch, "E236.2", {"start": v(9.9, 4.32) * mm, "end": v(10.58, 4.3) * mm});
            skLineSegment(sketch, "E236.3", {"start": v(8.67, 4.5) * mm, "end": v(9.23, 4.4) * mm});
            skLineSegment(sketch, "E236.4", {"start": v(8.37, 4.62) * mm, "end": v(8.67, 4.5) * mm});
            skLineSegment(sketch, "E236.5", {"start": v(9.75, 5.09) * mm, "end": v(9.09, 5.04) * mm});
            skLineSegment(sketch, "E236.6", {"start": v(9.09, 5.04) * mm, "end": v(8.6, 4.93) * mm});
            skLineSegment(sketch, "E237.2", {"start": v(12.57, 2.92) * mm, "end": v(11.37, 3.01) * mm});
            skLineSegment(sketch, "E237.3", {"start": v(10.83, 4.96) * mm, "end": v(10.4, 5.06) * mm});
            skLineSegment(sketch, "E237.4", {"start": v(10.4, 5.06) * mm, "end": v(9.75, 5.09) * mm});
            skLineSegment(sketch, "E237.5", {"start": v(11.03, 4.8) * mm, "end": v(10.83, 4.96) * mm});
            skLineSegment(sketch, "E237.6", {"start": v(10.58, 4.3) * mm, "end": v(10.86, 4.32) * mm});
            skLineSegment(sketch, "E238.0", {"start": v(10.86, 4.32) * mm, "end": v(11.01, 4.35) * mm});
            skLineSegment(sketch, "E238.2", {"start": v(11.1, 4.57) * mm, "end": v(11.03, 4.8) * mm});
            skLineSegment(sketch, "E238.3", {"start": v(11.01, 4.35) * mm, "end": v(11.08, 4.43) * mm});
            skLineSegment(sketch, "E238.5", {"start": v(11.08, 4.43) * mm, "end": v(11.1, 4.57) * mm});
            skLineSegment(sketch, "E239.0", {"start": v(8.6, 4.93) * mm, "end": v(8.4, 4.85) * mm});
            skLineSegment(sketch, "E240.0", {"start": v(8.3, 4.7) * mm, "end": v(8.37, 4.62) * mm});
            skLineSegment(sketch, "E240.1", {"start": v(8.3, 4.78) * mm, "end": v(8.3, 4.7) * mm});
            skLineSegment(sketch, "E240.3", {"start": v(8.4, 4.85) * mm, "end": v(8.3, 4.78) * mm});
            skLineSegment(sketch, "E241.0", {"start": v(7.93, 2.98) * mm, "end": v(7.61, 2.85) * mm});
            skLineSegment(sketch, "E241.1", {"start": v(13.57, 2.29) * mm, "end": v(13.34, 2.13) * mm});
            skLineSegment(sketch, "E241.2", {"start": v(14.13, 2.47) * mm, "end": v(13.68, 2.19) * mm});
            skLineSegment(sketch, "E241.3", {"start": v(9.5, 1.67) * mm, "end": v(8.52, 1.6) * mm});
            skLineSegment(sketch, "E241.4", {"start": v(13.47, 2.8) * mm, "end": v(12.57, 2.92) * mm});
            skLineSegment(sketch, "E241.5", {"start": v(10.47, 1.74) * mm, "end": v(9.5, 1.67) * mm});
            skLineSegment(sketch, "E241.6", {"start": v(13.68, 2.19) * mm, "end": v(13.01, 2) * mm});
            skLineSegment(sketch, "E241.7", {"start": v(7.61, 2.85) * mm, "end": v(7.18, 2.62) * mm});
            skLineSegment(sketch, "E241.8", {"start": v(12, 1.85) * mm, "end": v(10.47, 1.74) * mm});
            skLineSegment(sketch, "E241.9", {"start": v(8.32, 3.04) * mm, "end": v(7.93, 2.98) * mm});
            skLineSegment(sketch, "E241.10", {"start": v(13.57, 2.29) * mm, "end": v(13.78, 2.44) * mm});
            skLineSegment(sketch, "E241.11", {"start": v(6.43, 1.62) * mm, "end": v(6.61, 1.54) * mm});
            skLineSegment(sketch, "E241.12", {"start": v(13.9, 2.67) * mm, "end": v(13.47, 2.8) * mm});
            skLineSegment(sketch, "E241.13", {"start": v(6.61, 1.54) * mm, "end": v(6.87, 1.45) * mm});
            skLineSegment(sketch, "E241.14", {"start": v(8.52, 1.6) * mm, "end": v(7.66, 1.53) * mm});
            skLineSegment(sketch, "E241.15", {"start": v(7.66, 1.53) * mm, "end": v(7.03, 1.47) * mm});
            skLineSegment(sketch, "E241.16", {"start": v(8.97, 3.06) * mm, "end": v(8.32, 3.04) * mm});
            skLineSegment(sketch, "E241.17", {"start": v(10.06, 3.05) * mm, "end": v(8.97, 3.06) * mm});
            skLineSegment(sketch, "E241.18", {"start": v(6.47, 2.1) * mm, "end": v(6.29, 1.88) * mm});
            skLineSegment(sketch, "E241.19", {"start": v(7.18, 2.62) * mm, "end": v(6.78, 2.36) * mm});
            skLineSegment(sketch, "E241.20", {"start": v(13.01, 2) * mm, "end": v(12, 1.85) * mm});
            skLineSegment(sketch, "E241.23", {"start": v(6.78, 2.36) * mm, "end": v(6.47, 2.1) * mm});
            skLineSegment(sketch, "E242.0", {"start": v(13.78, 2.44) * mm, "end": v(13.91, 2.57) * mm});
            skLineSegment(sketch, "E243.0", {"start": v(13.91, 2.57) * mm, "end": v(13.9, 2.67) * mm});
            skLineSegment(sketch, "E244.0", {"start": v(13.34, 2.13) * mm, "end": v(13.26, 2.06) * mm});
            skLineSegment(sketch, "E245.0", {"start": v(6.29, 1.88) * mm, "end": v(6.25, 1.77) * mm});
            skLineSegment(sketch, "E245.1", {"start": v(6.25, 1.77) * mm, "end": v(6.3, 1.72) * mm});
            skLineSegment(sketch, "E245.2", {"start": v(6.3, 1.72) * mm, "end": v(6.43, 1.62) * mm});
            skSolve(sketch);
        }
        {
            var Q0;
            Q0=makeQuery(id+"F2.imprint","IMPRINT",FACE,{"disambiguationData":[TD([[makeQuery(id+"F2.imprint","IMPRINT",EDGE,{"derivedFrom":sQuery(id+"F2.wireOp",EDGE,"E234.4")}),1.0]])]});
            var Q1;
            Q1=makeQuery(id+"F2.imprint","IMPRINT",FACE,{"disambiguationData":[TD([[makeQuery(id+"F2.imprint","IMPRINT",EDGE,{"derivedFrom":sQuery(id+"F2.wireOp",EDGE,"E241.0")}),1.0]])]});
            var Q2;
            Q2=makeQuery(id+"F2.imprint","IMPRINT",FACE,{"disambiguationData":[TD([[makeQuery(id+"F2.imprint","IMPRINT",EDGE,{"derivedFrom":sQuery(id+"F2.wireOp",EDGE,"E236.3")}),1.0]])]});
            extrude(context, id + "F3", {"entities" : qUnion([Q0, Q1, Q2]), "operationType" : NewBodyOperationType.ADD, "depth" : 0.4 * mm, "offsetDistance" : 25 * mm});
        }
        {
            var Q0;
            Q0=makeQuery(id+"F1.opExtrude","CAP_EDGE",EDGE,{"disambiguationData":[OSD([sQuery(id+"F0.wireOp",EDGE,"E230")])],"isStart":true});
            var Q1;
            Q1=makeQuery(id+"F1.opExtrude","CAP_EDGE",EDGE,{"disambiguationData":[OSD([sQuery(id+"F0.wireOp",EDGE,"E229")])],"isStart":true});
            var Q2;
            Q2=makeQuery(id+"F1.opExtrude","CAP_EDGE",EDGE,{"disambiguationData":[OSD([sQuery(id+"F0.wireOp",EDGE,"E229")])],"isStart":false});
            var Q3;
            Q3=makeQuery(id+"F1.opExtrude","CAP_EDGE",EDGE,{"disambiguationData":[OSD([sQuery(id+"F0.wireOp",EDGE,"E230")])],"isStart":false});
            fillet(context, id + "F4", {"entities" : qUnion([Q0, Q1, Q2, Q3]), "radius" : 0.4 * mm, "tangentPropagation" : true, "allowEdgeOverflow" : false});
        }
        {
            var Q0;
            Q0=makeQuery(id+"F1.opExtrude","CAP_FACE",FACE,{"disambiguationData":[OSD([sQuery(id+"F0.wireOp",EDGE,"E0"),sQuery(id+"F0.wireOp",EDGE,"E1"),sQuery(id+"F0.wireOp",EDGE,"E2"),sQuery(id+"F0.wireOp",EDGE,"E3"),sQuery(id+"F0.wireOp",EDGE,"E4"),sQuery(id+"F0.wireOp",EDGE,"E5"),sQuery(id+"F0.wireOp",EDGE,"E6"),sQuery(id+"F0.wireOp",EDGE,"E7"),sQuery(id+"F0.wireOp",EDGE,"E8"),sQuery(id+"F0.wireOp",EDGE,"E9"),sQuery(id+"F0.wireOp",EDGE,"E10"),sQuery(id+"F0.wireOp",EDGE,"E11"),sQuery(id+"F0.wireOp",EDGE,"E12"),sQuery(id+"F0.wireOp",EDGE,"E13"),sQuery(id+"F0.wireOp",EDGE,"E14"),sQuery(id+"F0.wireOp",EDGE,"E15"),sQuery(id+"F0.wireOp",EDGE,"E16"),sQuery(id+"F0.wireOp",EDGE,"E17"),sQuery(id+"F0.wireOp",EDGE,"E18"),sQuery(id+"F0.wireOp",EDGE,"E19"),sQuery(id+"F0.wireOp",EDGE,"E20"),sQuery(id+"F0.wireOp",EDGE,"E21"),sQuery(id+"F0.wireOp",EDGE,"E22"),sQuery(id+"F0.wireOp",EDGE,"E23"),sQuery(id+"F0.wireOp",EDGE,"E24"),sQuery(id+"F0.wireOp",EDGE,"E25"),sQuery(id+"F0.wireOp",EDGE,"E26"),sQuery(id+"F0.wireOp",EDGE,"E27"),sQuery(id+"F0.wireOp",EDGE,"E28"),sQuery(id+"F0.wireOp",EDGE,"E29"),sQuery(id+"F0.wireOp",EDGE,"E30"),sQuery(id+"F0.wireOp",EDGE,"E31"),sQuery(id+"F0.wireOp",EDGE,"E32"),sQuery(id+"F0.wireOp",EDGE,"E33"),sQuery(id+"F0.wireOp",EDGE,"E34"),sQuery(id+"F0.wireOp",EDGE,"E35"),sQuery(id+"F0.wireOp",EDGE,"E36"),sQuery(id+"F0.wireOp",EDGE,"E37"),sQuery(id+"F0.wireOp",EDGE,"E38"),sQuery(id+"F0.wireOp",EDGE,"E39"),sQuery(id+"F0.wireOp",EDGE,"E40"),sQuery(id+"F0.wireOp",EDGE,"E41"),sQuery(id+"F0.wireOp",EDGE,"E42"),sQuery(id+"F0.wireOp",EDGE,"E43"),sQuery(id+"F0.wireOp",EDGE,"E44"),sQuery(id+"F0.wireOp",EDGE,"E45"),sQuery(id+"F0.wireOp",EDGE,"E46"),sQuery(id+"F0.wireOp",EDGE,"E47"),sQuery(id+"F0.wireOp",EDGE,"E48"),sQuery(id+"F0.wireOp",EDGE,"E49"),sQuery(id+"F0.wireOp",EDGE,"E50"),sQuery(id+"F0.wireOp",EDGE,"E51"),sQuery(id+"F0.wireOp",EDGE,"E52"),sQuery(id+"F0.wireOp",EDGE,"E53"),sQuery(id+"F0.wireOp",EDGE,"E54"),sQuery(id+"F0.wireOp",EDGE,"E55"),sQuery(id+"F0.wireOp",EDGE,"E56"),sQuery(id+"F0.wireOp",EDGE,"E57"),sQuery(id+"F0.wireOp",EDGE,"E58"),sQuery(id+"F0.wireOp",EDGE,"E59"),sQuery(id+"F0.wireOp",EDGE,"E60"),sQuery(id+"F0.wireOp",EDGE,"E61"),sQuery(id+"F0.wireOp",EDGE,"E62"),sQuery(id+"F0.wireOp",EDGE,"E63"),sQuery(id+"F0.wireOp",EDGE,"E64"),sQuery(id+"F0.wireOp",EDGE,"E65"),sQuery(id+"F0.wireOp",EDGE,"E66"),sQuery(id+"F0.wireOp",EDGE,"E67"),sQuery(id+"F0.wireOp",EDGE,"E68"),sQuery(id+"F0.wireOp",EDGE,"E69"),sQuery(id+"F0.wireOp",EDGE,"E70"),sQuery(id+"F0.wireOp",EDGE,"E71"),sQuery(id+"F0.wireOp",EDGE,"E72"),sQuery(id+"F0.wireOp",EDGE,"E73"),sQuery(id+"F0.wireOp",EDGE,"E74"),sQuery(id+"F0.wireOp",EDGE,"E75"),sQuery(id+"F0.wireOp",EDGE,"E76"),sQuery(id+"F0.wireOp",EDGE,"E77"),sQuery(id+"F0.wireOp",EDGE,"E78"),sQuery(id+"F0.wireOp",EDGE,"E79"),sQuery(id+"F0.wireOp",EDGE,"E80"),sQuery(id+"F0.wireOp",EDGE,"E81"),sQuery(id+"F0.wireOp",EDGE,"E82"),sQuery(id+"F0.wireOp",EDGE,"E83"),sQuery(id+"F0.wireOp",EDGE,"E84"),sQuery(id+"F0.wireOp",EDGE,"E85"),sQuery(id+"F0.wireOp",EDGE,"E86"),sQuery(id+"F0.wireOp",EDGE,"E87"),sQuery(id+"F0.wireOp",EDGE,"E88"),sQuery(id+"F0.wireOp",EDGE,"E89"),sQuery(id+"F0.wireOp",EDGE,"E90"),sQuery(id+"F0.wireOp",EDGE,"E91"),sQuery(id+"F0.wireOp",EDGE,"E92"),sQuery(id+"F0.wireOp",EDGE,"E93"),sQuery(id+"F0.wireOp",EDGE,"E94"),sQuery(id+"F0.wireOp",EDGE,"E95"),sQuery(id+"F0.wireOp",EDGE,"E96"),sQuery(id+"F0.wireOp",EDGE,"E97"),sQuery(id+"F0.wireOp",EDGE,"E98"),sQuery(id+"F0.wireOp",EDGE,"E99"),sQuery(id+"F0.wireOp",EDGE,"E100"),sQuery(id+"F0.wireOp",EDGE,"E101"),sQuery(id+"F0.wireOp",EDGE,"E102"),sQuery(id+"F0.wireOp",EDGE,"E103"),sQuery(id+"F0.wireOp",EDGE,"E104"),sQuery(id+"F0.wireOp",EDGE,"E105"),sQuery(id+"F0.wireOp",EDGE,"E106"),sQuery(id+"F0.wireOp",EDGE,"E107"),sQuery(id+"F0.wireOp",EDGE,"E108"),sQuery(id+"F0.wireOp",EDGE,"E109"),sQuery(id+"F0.wireOp",EDGE,"E110"),sQuery(id+"F0.wireOp",EDGE,"E111"),sQuery(id+"F0.wireOp",EDGE,"E112"),sQuery(id+"F0.wireOp",EDGE,"E113"),sQuery(id+"F0.wireOp",EDGE,"E114"),sQuery(id+"F0.wireOp",EDGE,"E115"),sQuery(id+"F0.wireOp",EDGE,"E116"),sQuery(id+"F0.wireOp",EDGE,"E117"),sQuery(id+"F0.wireOp",EDGE,"E118"),sQuery(id+"F0.wireOp",EDGE,"E119"),sQuery(id+"F0.wireOp",EDGE,"E120"),sQuery(id+"F0.wireOp",EDGE,"E121"),sQuery(id+"F0.wireOp",EDGE,"E122"),sQuery(id+"F0.wireOp",EDGE,"E123"),sQuery(id+"F0.wireOp",EDGE,"E124"),sQuery(id+"F0.wireOp",EDGE,"E125"),sQuery(id+"F0.wireOp",EDGE,"E126"),sQuery(id+"F0.wireOp",EDGE,"E127"),sQuery(id+"F0.wireOp",EDGE,"E128"),sQuery(id+"F0.wireOp",EDGE,"E129"),sQuery(id+"F0.wireOp",EDGE,"E130"),sQuery(id+"F0.wireOp",EDGE,"E131"),sQuery(id+"F0.wireOp",EDGE,"E132"),sQuery(id+"F0.wireOp",EDGE,"E133"),sQuery(id+"F0.wireOp",EDGE,"E134"),sQuery(id+"F0.wireOp",EDGE,"E135"),sQuery(id+"F0.wireOp",EDGE,"E229"),sQuery(id+"F0.wireOp",EDGE,"E230")])],"isStart":true});
            chamfer(context, id + "F5", {"entities" : qUnion([Q0]), "width" : 0.15 * mm, "tangentPropagation" : true});
        }
    });
